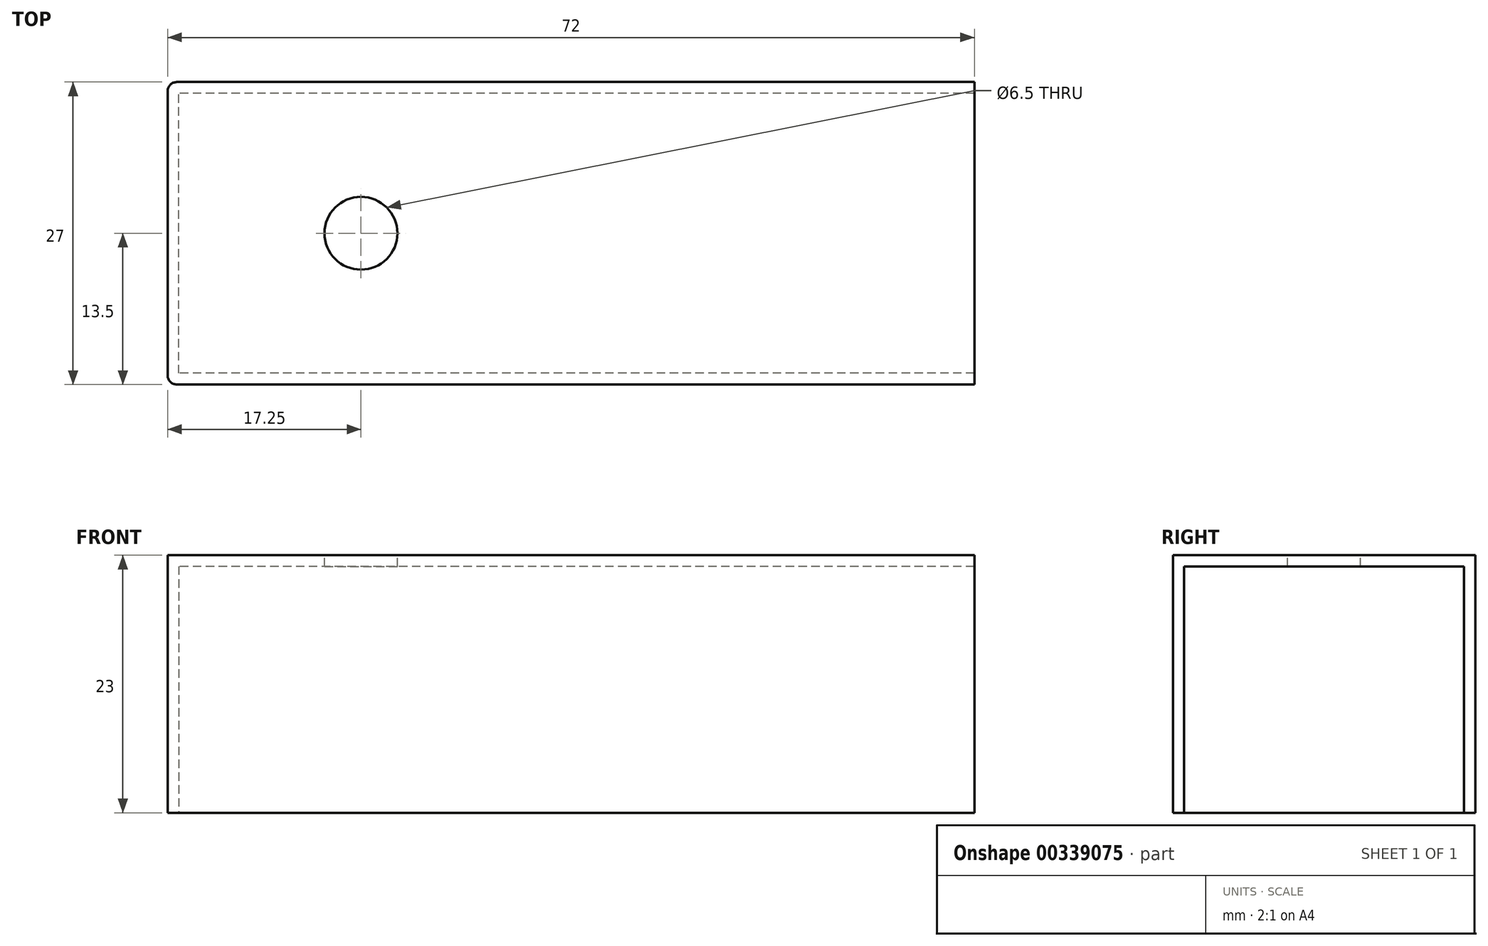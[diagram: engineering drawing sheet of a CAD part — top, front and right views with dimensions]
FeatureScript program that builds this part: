
annotation { "Feature Type Name" : "Feature", "Feature Type Description" : "" }
export const myFeature = defineFeature(function(context is Context, id is Id, definition is map)
    precondition{}
    {
        {
            var Q0;
            Q0=qCreatedBy(makeId("Front.planeOp"),FACE);
            var sketch = newSketch(context, id + "F0", { "sketchPlane" : qUnion([Q0])});
            skLineSegment(sketch, "E0.bottom", {"start": v(36, 12) * mm, "end": v(-36, 12) * mm});
            skLineSegment(sketch, "E0.top", {"start": v(36, -12) * mm, "end": v(-36, -12) * mm});
            skLineSegment(sketch, "E0.left", {"start": v(36, 12) * mm, "end": v(36, -12) * mm});
            skLineSegment(sketch, "E0.right", {"start": v(-36, 12) * mm, "end": v(-36, -12) * mm});
            skPoint(sketch, "E0.middle", {"position": v(0, 0) * mm});
            skSolve(sketch);
        }
        {
            var Q0;
            Q0 = qSketchRegion(id + "F0", true);
            extrude(context, id + "F1", {"entities" : qUnion([Q0]), "depth" : 27 * mm, "offsetDistance" : 25 * mm});
        }
        {
            var Q0;
            Q0=makeQuery(id+"F1.opExtrude","SWEPT_FACE",FACE,{"disambiguationData":[OSD([sQuery(id+"F0.wireOp",EDGE,"E0.left")])]});
            shell(context, id + "F2", {"entities" : qUnion([Q0]), "thickness" : 1 * mm});
        }
        {
            var Q0;
            Q0=makeQuery(id+"F1.opExtrude","SWEPT_FACE",FACE,{"disambiguationData":[OSD([sQuery(id+"F0.wireOp",EDGE,"E0.bottom")])]});
            var sketch = newSketch(context, id + "F3", { "sketchPlane" : qUnion([Q0])});
            skCircle(sketch, "E1", {"center": v(-18.75, -13.5) * mm, "radius": 3.25 * mm});
            skPoint(sketch, "E1.centerSnap0", {"position": v(-36, -13.5) * mm});
            skLineSegment(sketch, "E2", {"start": v(-36, -13.5) * mm, "end": v(36, -13.5) * mm, "construction": true});
            skSolve(sketch);
        }
        {
            var Q0;
            Q0=makeQuery(id+"F3.imprint","IMPRINT",FACE,{"disambiguationData":[TD([[makeQuery(id+"F3.imprint","IMPRINT",EDGE,{"derivedFrom":sQuery(id+"F3.wireOp",EDGE,"E1")}),1.0]])]});
            var Q1;
            Q1=makeQuery(id+"F3.imprint","IMPRINT",FACE,{"disambiguationData":[TD([[makeQuery(id+"F3.imprint","IMPRINT",EDGE,{"derivedFrom":sQuery(id+"F3.wireOp",EDGE,"f72dff70-d005-4f61-9351-71af8dcf48150.MirrorC")}),-1.0]])]});
            var Q2;
            Q2=makeQuery(id+"F3.imprint","IMPRINT",FACE,{"disambiguationData":[TD([[makeQuery(id+"F3.imprint","IMPRINT",EDGE,{"derivedFrom":sQuery(id+"F3.wireOp",EDGE,"9Myu96Tb-Zw78-1S8A-UgoA-B5o2QO1kPbBn")}),1.0]])]});
            extrude(context, id + "F4", {"entities" : qUnion([Q0, Q1, Q2]), "operationType" : NewBodyOperationType.REMOVE, "oppositeDirection" : true, "depth" : 25 * mm, "offsetDistance" : 25 * mm});
        }
        {
            var Q0;
            Q0=makeQuery(id+"F1.opExtrude","SWEPT_FACE",FACE,{"disambiguationData":[OSD([sQuery(id+"F0.wireOp",EDGE,"E0.top")])]});
            var sketch = newSketch(context, id + "F5", { "sketchPlane" : qUnion([Q0])});
            skLineSegment(sketch, "E3.bottom", {"start": v(-36, 27) * mm, "end": v(36, 27) * mm});
            skLineSegment(sketch, "E3.top", {"start": v(-36, 0) * mm, "end": v(36, 0) * mm});
            skLineSegment(sketch, "E3.left", {"start": v(-36, 27) * mm, "end": v(-36, 0) * mm});
            skLineSegment(sketch, "E3.right", {"start": v(36, 27) * mm, "end": v(36, 0) * mm});
            skSolve(sketch);
        }
        {
            var Q0;
            Q0=makeQuery(id+"F5.imprint","IMPRINT",FACE,{"disambiguationData":[TD([[makeQuery(id+"F5.imprint","IMPRINT",EDGE,{"derivedFrom":sQuery(id+"F5.wireOp",EDGE,"E3.bottom")}),1.0]])]});
            extrude(context, id + "F6", {"entities" : qUnion([Q0]), "operationType" : NewBodyOperationType.REMOVE, "oppositeDirection" : true, "depth" : 1 * mm, "offsetDistance" : 25 * mm});
        }
        {
            var Q0;
            Q0=makeQuery(id+"F1.opExtrude","SWEPT_FACE",FACE,{"disambiguationData":[OSD([sQuery(id+"F0.wireOp",EDGE,"E0.bottom")])]});
            var sketch = newSketch(context, id + "F7", { "sketchPlane" : qUnion([Q0])});
            skLineSegment(sketch, "E4.0.2", {"start": v(-36, -27) * mm, "end": v(36, -27) * mm});
            skPoint(sketch, "E5.middle.positionSnap0", {"position": v(-36, -13.5) * mm});
            skPoint(sketch, "E5.centerSnap0", {"position": v(-36, -13.5) * mm});
            skLineSegment(sketch, "E6", {"start": v(-18.75, -10.25) * mm, "end": v(36, -10.25) * mm});
            skLineSegment(sketch, "E7", {"start": v(-18.75, -16.75) * mm, "end": v(36, -16.75) * mm});
            skLineSegment(sketch, "E8", {"start": v(-36, -27) * mm, "end": v(-36, -1) * mm});
            skLineSegment(sketch, "E9", {"start": v(36, -27) * mm, "end": v(36, -1) * mm});
            skLineSegment(sketch, "E10", {"start": v(36, -1) * mm, "end": v(-36, -1) * mm});
            skSolve(sketch);
        }
        {
            var Q0;
            Q0=makeQuery(id+"F7.imprint","IMPRINT",FACE,{"disambiguationData":[TD([[makeQuery(id+"F7.imprint","IMPRINT",EDGE,{"derivedFrom":sQuery(id+"F7.wireOp",EDGE,"E4.0.0")}),1.0]])]});
            var Q1;
            {var subQ3=sQuery(id+"F7.wireOp",EDGE,"E4.0.2");Q1=makeQuery(id+"F7.imprint","IMPRINT",FACE,{"disambiguationData":[TD([[makeQuery(id+"F7.imprint","IMPRINT",EDGE,{"derivedFrom":subQ3}),-1.0]])]});}
            extrude(context, id + "F8", {"entities" : qUnion([Q0, Q1]), "depth" : 1 * mm, "offsetDistance" : 25 * mm});
        }
        {
            var Q0;
            Q0=makeQuery(id+"F1.opExtrude","CAP_EDGE",EDGE,{"disambiguationData":[OSD([sQuery(id+"F0.wireOp",EDGE,"E0.right")])],"isStart":false});
            var Q1;
            Q1=makeQuery(id+"F1.opExtrude","CAP_EDGE",EDGE,{"disambiguationData":[OSD([sQuery(id+"F0.wireOp",EDGE,"E0.right")])],"isStart":true});
            var Q2;
            Q2=makeQuery(id+"F8.opExtrude","SWEPT_EDGE",EDGE,{"disambiguationData":[OSD([sQuery(id+"F7.wireOp",EDGE,"E4.0.1"),sQuery(id+"F7.wireOp",EDGE,"E4.0.2")])]});
            var Q3;
            Q3=makeQuery(id+"F8.opExtrude","SWEPT_EDGE",EDGE,{"disambiguationData":[OSD([sQuery(id+"F7.wireOp",EDGE,"E4.0.0"),sQuery(id+"F7.wireOp",EDGE,"E4.0.1")])]});
            fillet(context, id + "F9", {"entities" : qUnion([Q0, Q1, Q2, Q3]), "radius" : .8 * mm, "allowEdgeOverflow" : false});
        }
        {
            var Q0;
            Q0=makeQuery(id+"F8.opExtrude","SWEPT_BODY",BODY,{"disambiguationData":[OSD([sQuery(id+"F3.wireOp",EDGE,"E1"),sQuery(id+"F7.wireOp",EDGE,"E4.0.2"),sQuery(id+"F7.wireOp",EDGE,"E6"),sQuery(id+"F7.wireOp",EDGE,"E7"),sQuery(id+"F7.wireOp",EDGE,"E8"),sQuery(id+"F7.wireOp",EDGE,"E9"),sQuery(id+"F7.wireOp",EDGE,"E10")])]});
            deleteBodies(context, id + "F10", {"entities" : qUnion([Q0])});
        }
    });
